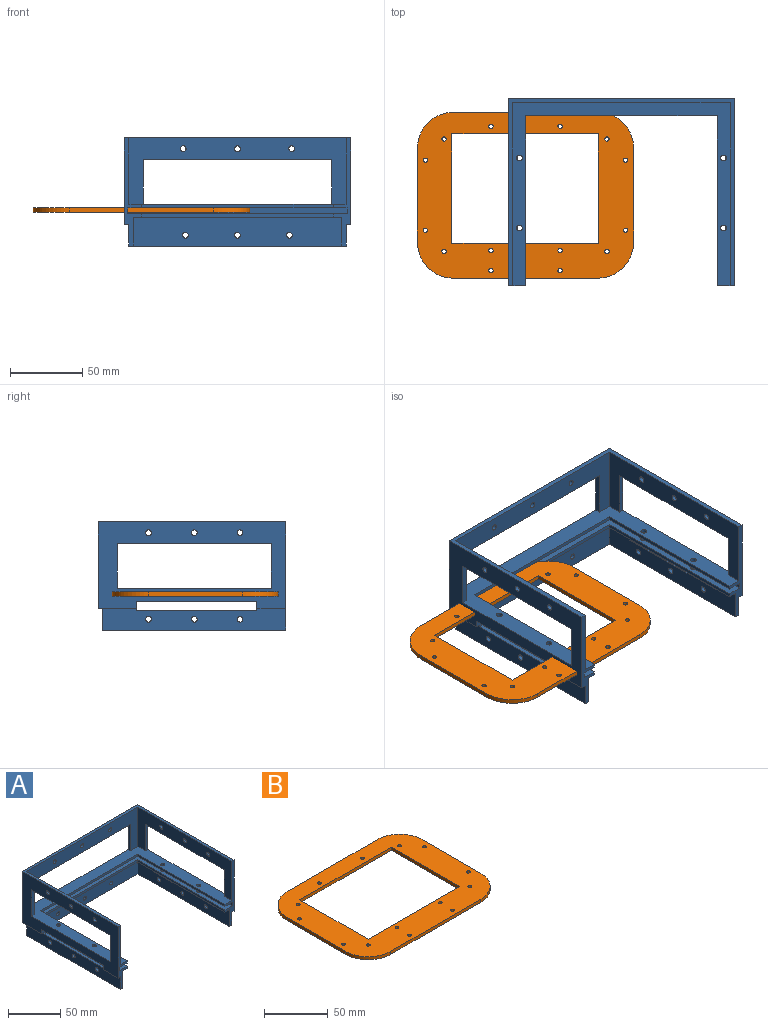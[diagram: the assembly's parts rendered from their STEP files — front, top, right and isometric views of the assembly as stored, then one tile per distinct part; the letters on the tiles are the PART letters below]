
ASSEMBLY  parts=2 mates=2
PART A: 81 faces, bbox 157x130x75 mm
  f0: plane 157x26.4mm, normal (0,0,-1), area 650.9mm2, adj f4,f6,f13,f30,f31,f32,f73,f78
  f1: plane 20x3.2mm, normal (0,0,-1), area 64mm2, adj f6,f16,f31,f75
  f2: plane 123.6x20mm, normal (-1,0,0), area 1890.9mm2, adj f7,f16,f33,f34,f44,f45,f46,f73
  f3: plane 123.6x20mm, normal (1,0,0), area 1890.9mm2, adj f7,f8,f33,f34,f41,f42,f43,f76
  f4: plane 130x60mm, normal (-1,0,0), area 4035.1mm2, adj f0,f7,f8,f13,f15,f17,f20,f38
  f5: plane 126.8x46mm, normal (1,0,0), area 2484.3mm2, adj f8,f14,f17,f20,f38,f39,f40,f47
  f6: plane 130x60mm, normal (1,0,0), area 4035.1mm2, adj f0,f1,f7,f13,f16,f17,f20,f35
  f7: plane 157x123.6mm, normal (0,0,-1), area 3150.7mm2, adj f2,f3,f4,f6,f8,f10,f16,f22
  f8: plane 75x12.2mm, normal (0,-1,0), area 298.2mm2, adj f3,f4,f5,f7,f9,f15,f17,f20
  f9: plane 117.8x2.5mm, normal (1,0,0), area 294.5mm2, adj f8,f20,f23,f28
  f10: plane 132.6x2.5mm, normal (0,-1,0), area 331.5mm2, adj f7,f22,f24,f29
  f11: plane 117.8x2.5mm, normal (-1,0,0), area 294.5mm2, adj f16,f20,f23,f28
  f12: plane 126.8x46mm, normal (-1,0,0), area 2484.3mm2, adj f14,f16,f17,f20,f35,f36,f37,f53
  f13: plane 157x60mm, normal (0,1,0), area 5333.7mm2, adj f0,f4,f6,f17,f18,f19,f20,f21
  f14: plane 150.6x46mm, normal (0,-1,0), area 2841.3mm2, adj f5,f12,f17,f18,f19,f20,f21,f50
  f15: plane 20x3.2mm, normal (0,0,-1), area 64mm2, adj f4,f8,f30,f76
  f16: plane 75x12.2mm, normal (0,-1,0), area 298.2mm2, adj f1,f2,f6,f7,f11,f12,f17,f20
  f17: plane 157x130mm, normal (0,0,1), area 1313.9mm2, adj f4,f5,f6,f8,f12,f13,f14,f16
  f18: plane 130.6x3.2mm, normal (0,0,-1), area 417.9mm2, adj f13,f14,f19,f21
  f19: plane 31x3.2mm, normal (1,0,0), area 99.2mm2, adj f13,f14,f18,f20
  f20: plane 157x130mm, normal (0,0,1), area 4527mm2, adj f4,f5,f6,f8,f9,f11,f12,f13
  f21: plane 31x3.2mm, normal (-1,0,0), area 99.2mm2, adj f13,f14,f18,f20
  f22: plane 117.8x2.5mm, normal (1,0,0), area 294.5mm2, adj f7,f8,f10,f29
  f23: plane 132.6x2.5mm, normal (0,-1,0), area 331.5mm2, adj f9,f11,f20,f28
  f24: plane 117.8x2.5mm, normal (-1,0,0), area 294.5mm2, adj f7,f10,f16,f29
  f25: plane 152x4mm, normal (0,-1,0), area 608mm2, adj f26,f27,f28,f29
  f26: plane 127.5x4mm, normal (1,0,0), area 510mm2, adj f8,f25,f28,f29
  f27: plane 127.5x4mm, normal (-1,0,0), area 510mm2, adj f16,f25,f28,f29
  f28: plane 152x127.5mm, normal (0,0,-1), area 3709.5mm2, adj f8,f9,f11,f16,f23,f25,f26,f27
  f29: plane 152x127.5mm, normal (0,0,1), area 3709.5mm2, adj f8,f10,f16,f22,f24,f25,f26,f27
  f30: plane 126.8x15mm, normal (-1,0,0), area 1738.9mm2, adj f0,f8,f15,f32,f33,f41,f42,f43
  f31: plane 126.8x15mm, normal (1,0,0), area 1738.9mm2, adj f0,f1,f16,f32,f33,f44,f45,f46
  f32: plane 150.6x15mm, normal (0,1,0), area 2221.3mm2, adj f0,f30,f31,f33,f68,f69,f70
  f33: plane 150.6x126.8mm, normal (0,0,-1), area 1273mm2, adj f2,f3,f8,f16,f30,f31,f32,f34
  f34: plane 144.2x20mm, normal (0,-1,0), area 2846.3mm2, adj f2,f3,f7,f33,f68,f69,f70
  f35: plane 106.8x3.2mm, normal (0,0,-1), area 341.8mm2, adj f6,f12,f36,f37
  f36: plane 31x3.2mm, normal (0,-1,0), area 99.2mm2, adj f6,f12,f20,f35
  f37: plane 31x3.2mm, normal (0,1,0), area 99.2mm2, adj f6,f12,f20,f35
  f38: plane 106.8x3.2mm, normal (0,0,-1), area 341.8mm2, adj f4,f5,f39,f40
  f39: plane 31x3.2mm, normal (0,1,0), area 99.2mm2, adj f4,f5,f20,f38
  f40: plane 31x3.2mm, normal (0,-1,0), area 99.2mm2, adj f4,f5,f20,f38
  f41: cylinder r=2mm len=4mm, axis (-1,0,0), area 40.2mm2, adj f3,f30
  f42: cylinder r=2mm len=4mm, axis (-1,0,0), area 40.2mm2, adj f3,f30
  f43: cylinder r=2mm len=4mm, axis (-1,0,0), area 40.2mm2, adj f3,f30
  f44: cylinder r=2mm len=4mm, axis (1,0,0), area 40.2mm2, adj f2,f31
  f45: cylinder r=2mm len=4mm, axis (1,0,0), area 40.2mm2, adj f2,f31
  f46: cylinder r=2mm len=4mm, axis (1,0,0), area 40.2mm2, adj f2,f31
  f47: cylinder r=2mm len=4mm, axis (1,0,0), area 40.2mm2, adj f4,f5
  f48: cylinder r=2mm len=4mm, axis (1,0,0), area 40.2mm2, adj f4,f5
  f49: cylinder r=2mm len=4mm, axis (1,0,0), area 40.2mm2, adj f4,f5
  f50: cylinder r=2mm len=4mm, axis (0,-1,0), area 40.2mm2, adj f13,f14
  f51: cylinder r=2mm len=4mm, axis (0,-1,0), area 40.2mm2, adj f13,f14
  f52: cylinder r=2mm len=4mm, axis (0,-1,0), area 40.2mm2, adj f13,f14
  f53: cylinder r=2mm len=4mm, axis (-1,0,0), area 40.2mm2, adj f6,f12
  f54: cylinder r=2mm len=4mm, axis (-1,0,0), area 40.2mm2, adj f6,f12
  f55: cylinder r=2mm len=4mm, axis (-1,0,0), area 40.2mm2, adj f6,f12
  f56: cone r=0mm half-angle=59deg, axis (0,0,1), area 1.7mm2, adj f57,f79
  f57: cylinder r=2mm len=4mm, axis (0,0,1), area 31.4mm2, adj f7,f29,f56
  f58: cone r=0mm half-angle=59deg, axis (0,0,1), area 1.7mm2, adj f59,f80
  f59: cylinder r=2mm len=4mm, axis (0,0,1), area 31.4mm2, adj f7,f29,f58
  f60: cone r=0mm half-angle=59deg, axis (0,0,1), area 1.7mm2, adj f61,f71
  f61: cylinder r=2mm len=4mm, axis (0,0,1), area 31.4mm2, adj f7,f29,f60
  f62: cone r=0mm half-angle=59deg, axis (0,0,1), area 1.7mm2, adj f63,f72
  f63: cylinder r=2mm len=4mm, axis (0,0,1), area 31.4mm2, adj f7,f29,f62
  f64: cylinder r=2mm len=4mm, axis (0,0,1), area 31.4mm2, adj f20,f28
  f65: cylinder r=2mm len=4mm, axis (0,0,1), area 31.4mm2, adj f20,f28
  f66: cylinder r=2mm len=4mm, axis (0,0,1), area 31.4mm2, adj f20,f28
  f67: cylinder r=2mm len=4mm, axis (0,0,1), area 31.4mm2, adj f20,f28
  f68: cylinder r=2mm len=4mm, axis (0,-1,0), area 40.2mm2, adj f32,f34
  f69: cylinder r=2mm len=4mm, axis (0,-1,0), area 40.2mm2, adj f32,f34
  f70: cylinder r=2mm len=4mm, axis (0,-1,0), area 40.2mm2, adj f32,f34
  f71: extruded ~6.4x3.04mm, area 20.3mm2, adj f6,f7,f60
  f72: extruded ~6.4x3.04mm, area 20.3mm2, adj f6,f7,f62
  f73: plane 6.5x6.4mm, normal (0,-1,0), area 36.8mm2, adj f0,f2,f6,f7,f31,f74
  f74: plane 83.6x3.2mm, normal (0,0,1), area 267.5mm2, adj f2,f31,f73,f75
  f75: plane 6.5x6.4mm, normal (0,1,0), area 36.8mm2, adj f1,f2,f6,f7,f31,f74
  f76: plane 6.5x6.4mm, normal (0,1,0), area 36.8mm2, adj f3,f4,f7,f15,f30,f77
  f77: plane 83.6x3.2mm, normal (0,0,1), area 267.5mm2, adj f3,f30,f76,f78
  f78: plane 6.5x6.4mm, normal (0,-1,0), area 36.8mm2, adj f0,f3,f4,f7,f30,f77
  f79: extruded ~6.4x3.04mm, area 20.3mm2, adj f4,f7,f56
  f80: extruded ~6.4x3.04mm, area 20.3mm2, adj f4,f7,f58
PART B: 28 faces, bbox 150x115x3 mm
  f0: plane 150x115mm, normal (0,0,-1), area 8915.8mm2, adj f2,f3,f4,f5,f6,f7,f8,f9
  f1: plane 150x115mm, normal (0,0,1), area 8915.8mm2, adj f2,f3,f4,f5,f6,f7,f8,f9
  f2: cylinder r=25mm len=25mm, axis (0,0,-1), area 117.8mm2, adj f0,f1,f3,f9
  f3: plane 100x3mm, normal (0,1,0), area 300mm2, adj f0,f1,f2,f4
  f4: cylinder r=25mm len=25mm, axis (0,0,-1), area 117.8mm2, adj f0,f1,f3,f5
  f5: plane 65x3mm, normal (-1,0,0), area 195mm2, adj f0,f1,f4,f6
  f6: cylinder r=25mm len=25mm, axis (0,0,-1), area 117.8mm2, adj f0,f1,f5,f7
  f7: plane 100x3mm, normal (0,-1,0), area 300mm2, adj f0,f1,f6,f8
  f8: cylinder r=25mm len=25mm, axis (0,0,-1), area 117.8mm2, adj f0,f1,f7,f9
  f9: plane 65x3mm, normal (1,0,0), area 195mm2, adj f0,f1,f2,f8
  f10: cylinder r=1.5mm len=3mm, axis (0,0,-1), area 28.3mm2, adj f0,f1
  f11: cylinder r=1.5mm len=3mm, axis (0,0,-1), area 28.3mm2, adj f0,f1
  f12: cylinder r=1.5mm len=3mm, axis (0,0,-1), area 28.3mm2, adj f0,f1
  f13: cylinder r=1.5mm len=3mm, axis (0,0,-1), area 28.3mm2, adj f0,f1
  f14: cylinder r=1.5mm len=3mm, axis (0,0,-1), area 28.3mm2, adj f0,f1
  f15: cylinder r=1.5mm len=3mm, axis (0,0,-1), area 28.3mm2, adj f0,f1
  f16: cylinder r=1.5mm len=3mm, axis (0,0,-1), area 28.3mm2, adj f0,f1
  f17: cylinder r=1.5mm len=3mm, axis (0,0,-1), area 28.3mm2, adj f0,f1
  f18: plane 101.5x3mm, normal (0,-1,0), area 304.5mm2, adj f0,f1,f19,f21
  f19: plane 75.85x3mm, normal (1,0,0), area 227.5mm2, adj f0,f1,f18,f20
  f20: plane 101.5x3mm, normal (0,1,0), area 304.5mm2, adj f0,f1,f19,f21
  f21: plane 75.85x3mm, normal (-1,0,0), area 227.5mm2, adj f0,f1,f18,f20
  f22: cylinder r=1.5mm len=3mm, axis (0,0,1), area 28.3mm2, adj f0,f1
  f23: cylinder r=1.5mm len=3mm, axis (0,0,1), area 28.3mm2, adj f0,f1
  f24: cylinder r=1.5mm len=3mm, axis (0,0,1), area 28.3mm2, adj f0,f1
  f25: cylinder r=1.5mm len=3mm, axis (0,0,1), area 28.3mm2, adj f0,f1
  f26: cylinder r=1.5mm len=3mm, axis (0,0,1), area 28.3mm2, adj f0,f1
  f27: cylinder r=1.5mm len=3mm, axis (0,0,1), area 28.3mm2, adj f0,f1
PLACE A t=(-12.3,-24.36,56.26)mm
PLACE B t=(-78.81,-26.57,4.76)mm
MATE parallel B.f1 <-> A.f28  axis (0,0,1) through (-78.6,-30.46,7.76)mm
MATE fastened B.f1 <-> A.f28  axis (0,0,1) through (-78.6,-30.46,7.76)mm
